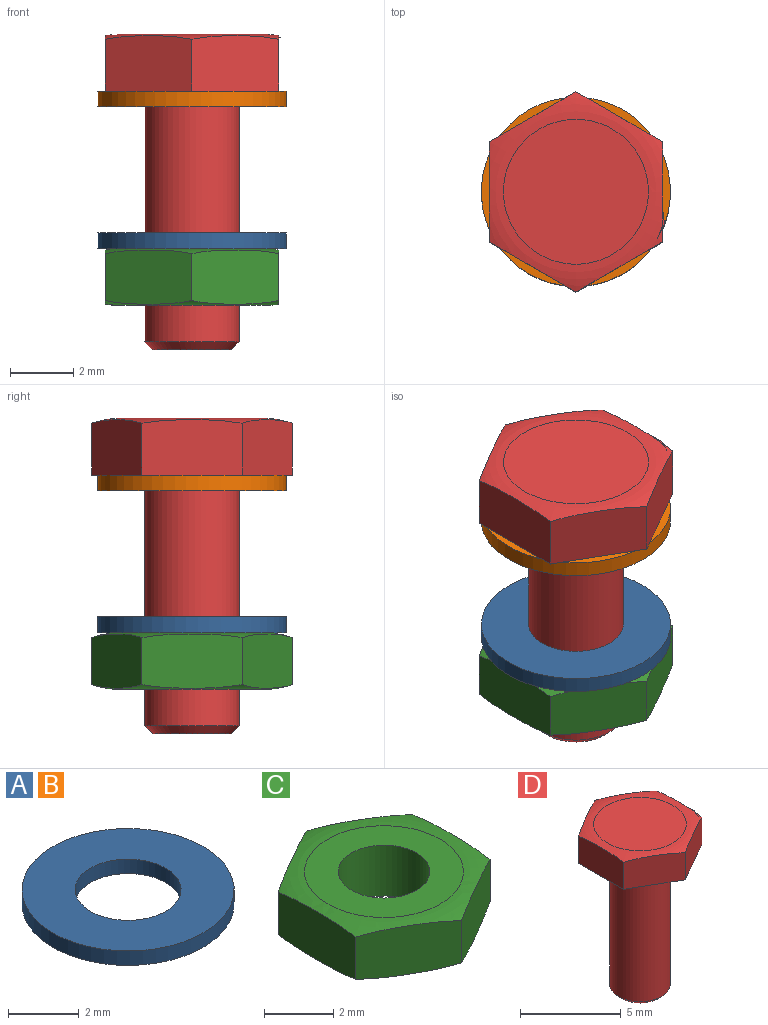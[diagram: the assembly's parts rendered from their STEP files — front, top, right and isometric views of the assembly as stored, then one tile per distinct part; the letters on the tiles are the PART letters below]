
ASSEMBLY  parts=4 mates=3
PART A: 4 faces, bbox 6x6x0.5 mm
  f0: cylinder r=1.5mm len=3mm, axis (0,0,-1), area 4.7mm2, adj f2,f3
  f1: cylinder r=3mm len=6mm, axis (0,0,-1), area 9.4mm2, adj f2,f3
  f2: plane 6x6mm, normal (0,0,1), area 21.2mm2, adj f0,f1
  f3: plane 6x6mm, normal (0,0,-1), area 21.2mm2, adj f0,f1
PART B: same geometry as A
PART C: 11 faces, bbox 6.6x6.6x2 mm
  f0: plane 4.6x4.6mm, normal (0,0,1), area 11.1mm2, adj f7,f10
  f1: plane 4.6x4.6mm, normal (0,0,-1), area 11.1mm2, adj f7,f9
  f2: plane 3.42x1.96mm, normal (1,0,0), area 5.2mm2, adj f3,f8,f9,f10
  f3: plane 2.75x1.72mm, normal (0.5,0.87,0), area 5.2mm2, adj f2,f4,f9,f10
  f4: plane 2.75x1.72mm, normal (-0.5,0.87,0), area 5.2mm2, adj f3,f5,f9,f10
  f5: plane 3.18x1.72mm, normal (-1,0,0), area 5.2mm2, adj f4,f6,f9,f10
  f6: plane 2.75x1.72mm, normal (-0.5,-0.87,0), area 5.2mm2, adj f5,f8,f9,f10
  f7: cylinder r=1.32mm len=2.65mm, axis (0,0,-1), area 15mm2, adj f0,f1
  f8: plane 2.75x1.72mm, normal (0.5,-0.87,0), area 5.2mm2, adj f2,f6,f9,f10
  f9: torus R=2.3mm, axis (0,0,1), area 9.9mm2, adj f1,f2,f3,f4,f5,f6,f8
  f10: torus R=2.3mm, axis (0,0,-1), area 9.9mm2, adj f0,f2,f3,f4,f5,f6,f8
PART D: 12 faces, bbox 6.6x6.6x10.2 mm
  f0: plane 3.42x2mm, normal (1,0,0), area 5.5mm2, adj f1,f5,f6,f7
  f1: plane 2.75x1.76mm, normal (0.5,0.87,0), area 5.5mm2, adj f0,f2,f6,f7
  f2: plane 2.75x1.76mm, normal (-0.5,0.87,0), area 5.5mm2, adj f1,f3,f6,f7
  f3: plane 3.18x1.76mm, normal (-1,0,0), area 5.5mm2, adj f2,f4,f6,f7
  f4: plane 2.75x1.76mm, normal (-0.5,-0.87,0), area 5.5mm2, adj f3,f5,f6,f7
  f5: plane 2.75x1.76mm, normal (0.5,-0.87,0), area 5.5mm2, adj f0,f4,f6,f7
  f6: plane 6.35x5.5mm, normal (0,0,-1), area 19.1mm2, adj f0,f1,f2,f3,f4,f5,f9
  f7: torus R=2.3mm, axis (0,0,1), area 9.9mm2, adj f0,f1,f2,f3,f4,f5,f8
  f8: plane 4.6x4.6mm, normal (0,0,1), area 16.6mm2, adj f7
  f9: cylinder r=1.5mm len=7.95mm, axis (0,0,1), area 74.9mm2, adj f6,f11
  f10: plane 2.5x2.5mm, normal (0,0,-1), area 4.9mm2, adj f11
  f11: cone r=1.5mm half-angle=45deg, axis (0,0,1), area 3.1mm2, adj f9,f10
PLACE A t=(-10.16,14.39,-5)mm
PLACE B t=(-10.16,14.39,-0.5)mm
PLACE C t=(-10.16,0,-6.8)mm
PLACE D at identity
MATE fastened B.f0 <-> D.f7  axis (0,0,1) through (-10.16,0,0)mm
MATE fastened A.f0 <-> B.f0  axis (0,0,1) through (-10.16,0,-4.5)mm
MATE fastened C.f7 <-> A.f0  axis (0,0,1) through (-10.16,0,-5)mm
